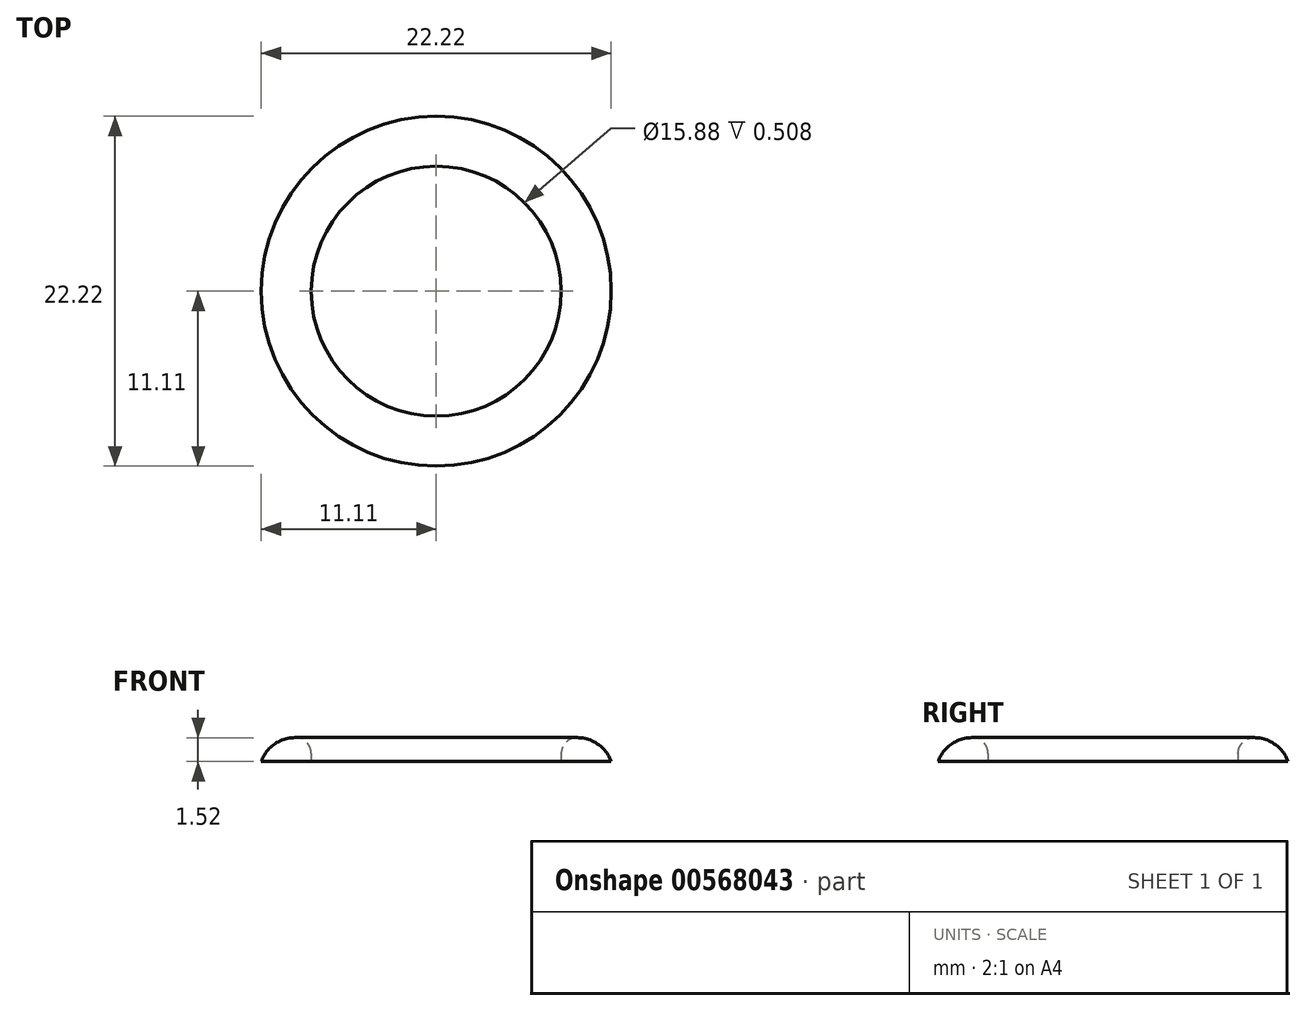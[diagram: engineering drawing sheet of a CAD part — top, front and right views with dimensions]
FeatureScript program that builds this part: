
annotation { "Feature Type Name" : "Feature", "Feature Type Description" : "" }
export const myFeature = defineFeature(function(context is Context, id is Id, definition is map)
    precondition{}
    {
        {
            var Q0;
            Q0=qCreatedBy(makeId("Top.planeOp"),FACE);
            var sketch = newSketch(context, id + "F0", { "sketchPlane" : qUnion([Q0])});
            skCircle(sketch, "E0", {"center": v(0, 0) * mm, "radius": 11.11 * mm});
            skCircle(sketch, "E1", {"center": v(0, 0) * mm, "radius": 7.94 * mm});
            skSolve(sketch);
        }
        {
            var Q0;
            Q0=makeQuery(id+"F0.imprint","IMPRINT",FACE,{"disambiguationData":[TD([[makeQuery(id+"F0.imprint","IMPRINT",EDGE,{"derivedFrom":sQuery(id+"F0.wireOp",EDGE,"E0")}),1.0]])]});
            extrude(context, id + "F1", {"entities" : qUnion([Q0]), "depth" : 1.52 * mm, "offsetDistance" : 25.4 * mm});
        }
        {
            var Q0;
            Q0=makeQuery(id+"F1.opExtrude","CAP_EDGE",EDGE,{"disambiguationData":[OSD([sQuery(id+"F0.wireOp",EDGE,"E0")])],"isStart":false});
            fillet(context, id + "F2", {"entities" : qUnion([Q0]), "radius" : 2.3 * mm, "tangentPropagation" : true, "allowEdgeOverflow" : false});
        }
        {
            var Q0;
            Q0=makeQuery(id+"F1.opExtrude","CAP_EDGE",EDGE,{"disambiguationData":[OSD([sQuery(id+"F0.wireOp",EDGE,"E1")])],"isStart":false});
            fillet(context, id + "F3", {"entities" : qUnion([Q0]), "radius" : 1.02 * mm, "tangentPropagation" : true, "allowEdgeOverflow" : false});
        }
    });
